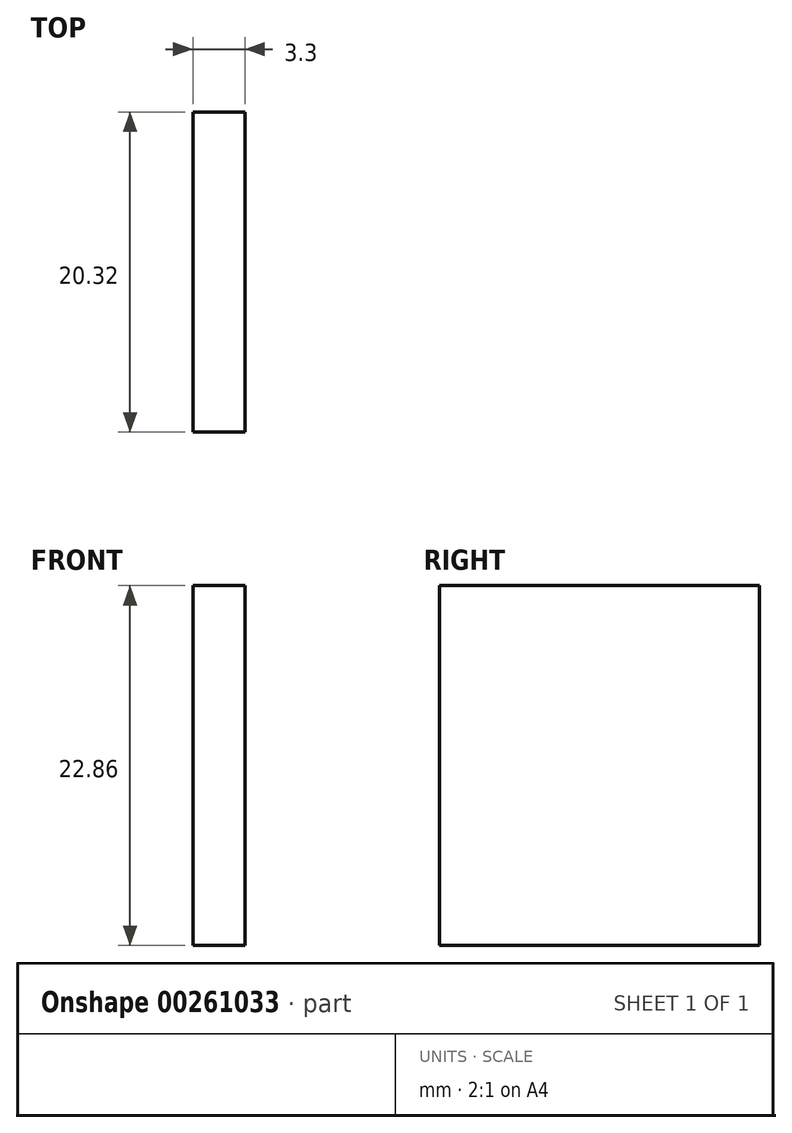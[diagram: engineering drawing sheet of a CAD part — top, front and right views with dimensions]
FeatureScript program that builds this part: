
annotation { "Feature Type Name" : "Feature", "Feature Type Description" : "" }
export const myFeature = defineFeature(function(context is Context, id is Id, definition is map)
    precondition{}
    {
        {
            var Q0;
            Q0=qCreatedBy(makeId("Right.planeOp"),FACE);
            var sketch = newSketch(context, id + "F0", { "sketchPlane" : qUnion([Q0])});
            skLineSegment(sketch, "E0.bottom", {"start": v(8.34, 11.43) * mm, "end": v(-11.98, 11.43) * mm});
            skLineSegment(sketch, "E0.top", {"start": v(8.34, -11.43) * mm, "end": v(-11.98, -11.43) * mm});
            skLineSegment(sketch, "E0.left", {"start": v(8.34, 11.43) * mm, "end": v(8.34, -11.43) * mm});
            skLineSegment(sketch, "E0.right", {"start": v(-11.98, 11.43) * mm, "end": v(-11.98, -11.43) * mm});
            skPoint(sketch, "E0.middle", {"position": v(-1.82, 0) * mm});
            skSolve(sketch);
        }
        {
            var Q0;
            Q0 = qSketchRegion(id + "F0", true);
            extrude(context, id + "F1", {"entities" : qUnion([Q0]), "depth" : 3.3 * mm});
        }
    });
